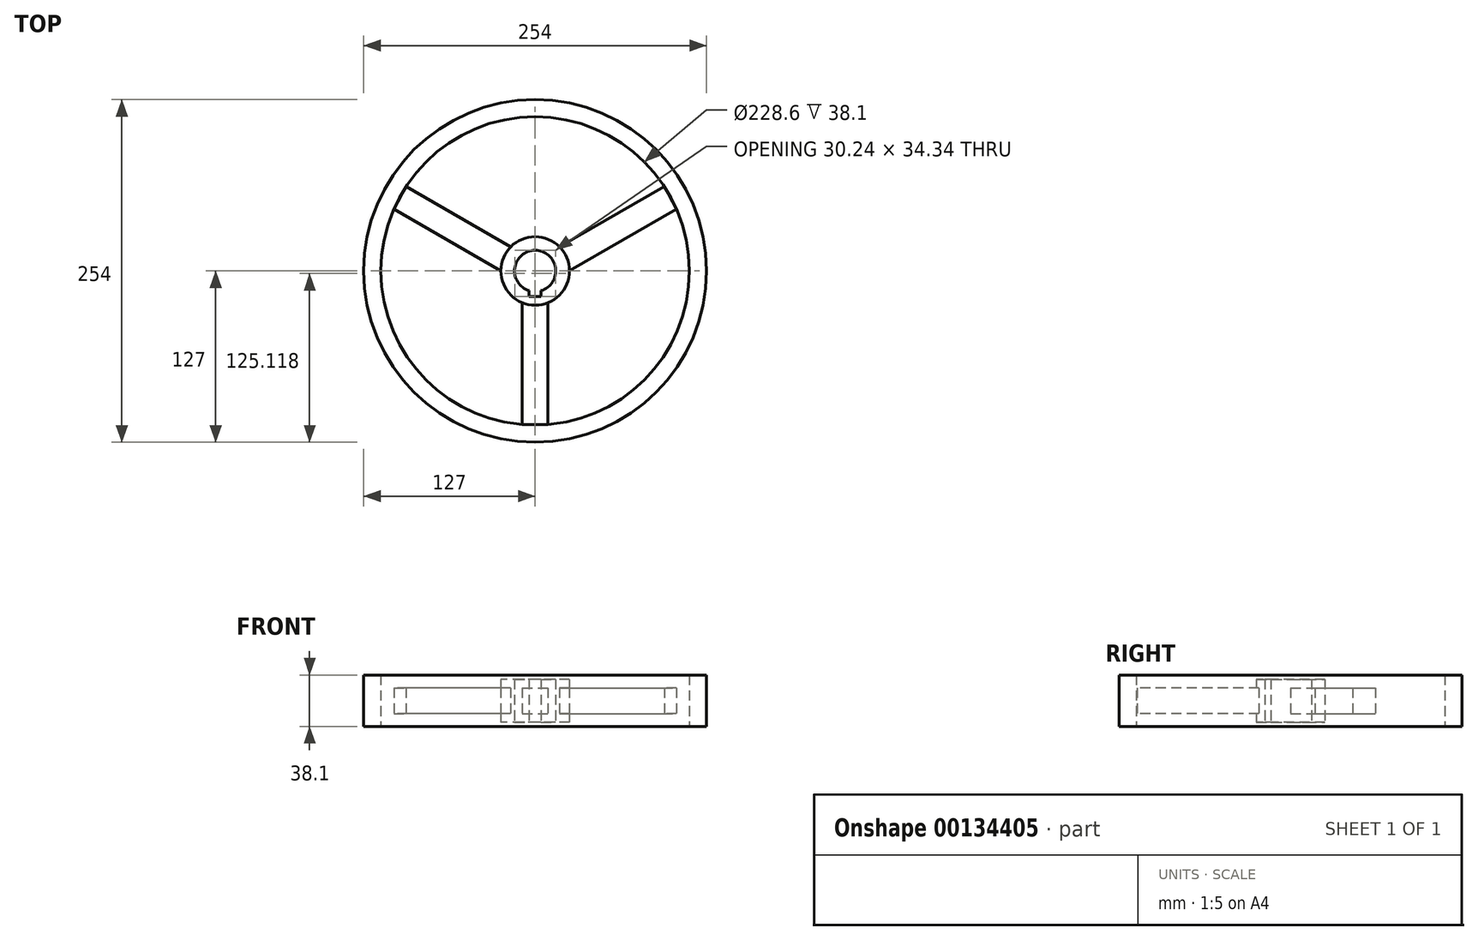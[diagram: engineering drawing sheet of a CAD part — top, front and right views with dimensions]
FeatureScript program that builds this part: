
annotation { "Feature Type Name" : "Feature", "Feature Type Description" : "" }
export const myFeature = defineFeature(function(context is Context, id is Id, definition is map)
    precondition{}
    {
        {
            var Q0;
            Q0=qCreatedBy(makeId("Top.planeOp"),FACE);
            var sketch = newSketch(context, id + "F0", { "sketchPlane" : qUnion([Q0])});
            skCircle(sketch, "E0", {"center": v(0, 0) * mm, "radius": 127 * mm});
            skCircle(sketch, "E1", {"center": v(0, 0) * mm, "radius": 114.3 * mm});
            skCircle(sketch, "E2", {"center": v(0, 0) * mm, "radius": 25.4 * mm});
            skArc(sketch, "E3", {"start": v(4.45, -14.62) * mm, "mid": v(0, 15.29) * mm, "end": v(-4.44, -14.62) * mm});
            skLineSegment(sketch, "E4", {"start": v(-25.4, 0) * mm, "end": v(-104.72, 45.8) * mm});
            skLineSegment(sketch, "E5", {"start": v(-18.13, 17.8) * mm, "end": v(-95.66, 62.55) * mm});
            skLineSegment(sketch, "E6", {"start": v(-9.53, -23.55) * mm, "end": v(-9.53, -113.9) * mm});
            skLineSegment(sketch, "E7", {"start": v(9.52, -23.55) * mm, "end": v(9.52, -113.9) * mm});
            skLineSegment(sketch, "E8", {"start": v(-4.45, -14.62) * mm, "end": v(-4.45, -19.05) * mm});
            skLineSegment(sketch, "E9", {"start": v(4.45, -14.62) * mm, "end": v(4.45, -19.05) * mm});
            skLineSegment(sketch, "E10", {"start": v(4.45, -19.05) * mm, "end": v(-4.45, -19.05) * mm});
            skLineSegment(sketch, "E11", {"start": v(-104.72, 45.8) * mm, "end": v(-95.66, 62.55) * mm});
            skLineSegment(sketch, "E12", {"start": v(-9.53, -113.9) * mm, "end": v(9.52, -113.9) * mm});
            skLineSegment(sketch, "E13", {"start": v(-25.4, 0) * mm, "end": v(-18.13, 17.8) * mm});
            skLineSegment(sketch, "E14", {"start": v(-9.53, -23.55) * mm, "end": v(9.52, -23.55) * mm});
            skLineSegment(sketch, "E15.MirrorCS", {"start": v(25.4, 0) * mm, "end": v(18.13, 17.8) * mm});
            skLineSegment(sketch, "E16.MirrorCS", {"start": v(18.13, 17.8) * mm, "end": v(95.66, 62.55) * mm});
            skLineSegment(sketch, "E17.MirrorCS", {"start": v(25.4, 0) * mm, "end": v(104.72, 45.8) * mm});
            skLineSegment(sketch, "E18.MirrorCS", {"start": v(104.72, 45.8) * mm, "end": v(95.66, 62.55) * mm});
            skSolve(sketch);
        }
        {
            var Q0;
            Q0=makeQuery(id+"F0.imprint","IMPRINT",FACE,{"disambiguationData":[TD([[makeQuery(id+"F0.imprint","IMPRINT",EDGE,{"derivedFrom":sQuery(id+"F0.wireOp",EDGE,"E0")}),1.0]])]});
            extrude(context, id + "F1", {"entities" : qUnion([Q0]), "endBound" : BoundingType.SYMMETRIC, "depth" : 38.1 * mm});
        }
        {
            var Q0;
            Q0=makeQuery(id+"F0.imprint","IMPRINT",FACE,{"disambiguationData":[TD([[makeQuery(id+"F0.imprint","IMPRINT",EDGE,{"derivedFrom":sQuery(id+"F0.wireOp",EDGE,"E3")}),-1.0]])]});
            var Q1;
            {var subQ0=sQuery(id+"F0.wireOp",EDGE,"E13");Q1=makeQuery(id+"F0.imprint","IMPRINT",FACE,{"disambiguationData":[TD([[makeQuery(id+"F0.imprint","IMPRINT",EDGE,{"derivedFrom":subQ0}),1.0]])]});}
            var Q2;
            {var subQ0=sQuery(id+"F0.wireOp",EDGE,"E15.MirrorCS");Q2=makeQuery(id+"F0.imprint","IMPRINT",FACE,{"disambiguationData":[TD([[makeQuery(id+"F0.imprint","IMPRINT",EDGE,{"derivedFrom":subQ0}),-1.0]])]});}
            var Q3;
            {var subQ0=sQuery(id+"F0.wireOp",EDGE,"E14");Q3=makeQuery(id+"F0.imprint","IMPRINT",FACE,{"disambiguationData":[TD([[makeQuery(id+"F0.imprint","IMPRINT",EDGE,{"derivedFrom":subQ0}),-1.0]])]});}
            extrude(context, id + "F2", {"entities" : qUnion([Q0, Q1, Q2, Q3]), "operationType" : NewBodyOperationType.ADD, "endBound" : BoundingType.SYMMETRIC, "depth" : 31.75 * mm});
        }
        {
            var Q0;
            {var subQ1=sQuery(id+"F0.wireOp",EDGE,"E4");Q0=makeQuery(id+"F0.imprint","IMPRINT",FACE,{"disambiguationData":[TD([[makeQuery(id+"F0.imprint","IMPRINT",EDGE,{"derivedFrom":subQ1}),-1.0]])]});}
            var Q1;
            {var subQ3=sQuery(id+"F0.wireOp",EDGE,"E16.MirrorCS");Q1=makeQuery(id+"F0.imprint","IMPRINT",FACE,{"disambiguationData":[TD([[makeQuery(id+"F0.imprint","IMPRINT",EDGE,{"derivedFrom":subQ3}),-1.0]])]});}
            var Q2;
            {var subQ1=sQuery(id+"F0.wireOp",EDGE,"E6");Q2=makeQuery(id+"F0.imprint","IMPRINT",FACE,{"disambiguationData":[TD([[makeQuery(id+"F0.imprint","IMPRINT",EDGE,{"derivedFrom":subQ1}),1.0]])]});}
            extrude(context, id + "F3", {"entities" : qUnion([Q0, Q1, Q2]), "operationType" : NewBodyOperationType.ADD, "endBound" : BoundingType.SYMMETRIC, "depth" : 19.05 * mm});
        }
    });
